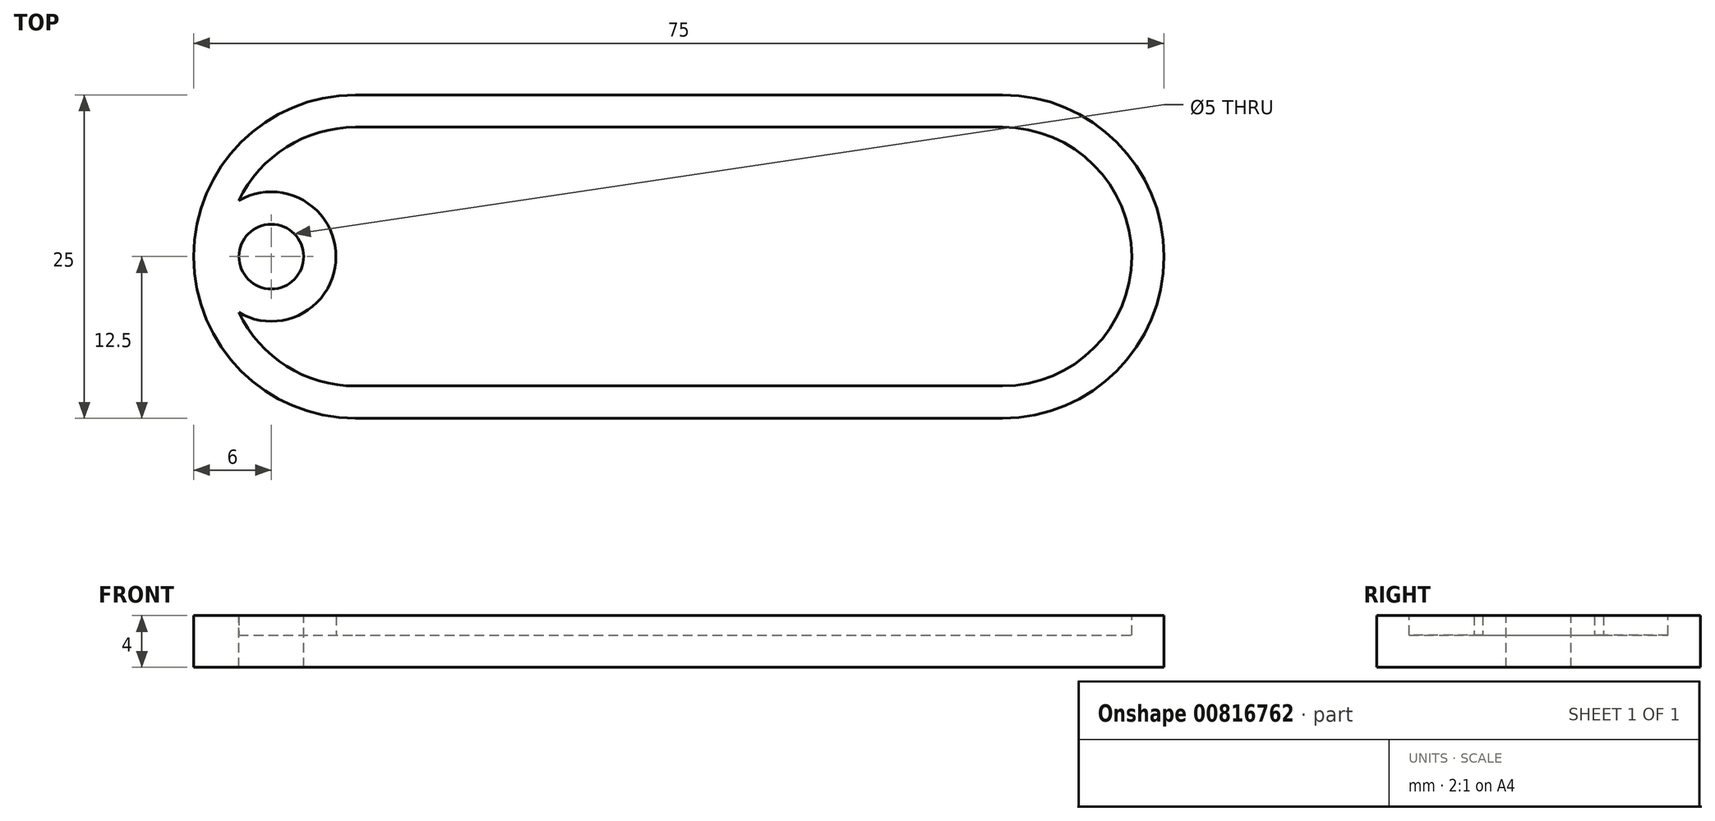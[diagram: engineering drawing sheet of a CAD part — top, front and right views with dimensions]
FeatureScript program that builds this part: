
annotation { "Feature Type Name" : "Feature", "Feature Type Description" : "" }
export const myFeature = defineFeature(function(context is Context, id is Id, definition is map)
    precondition{}
    {
        {
            var Q0;
            Q0=qCreatedBy(makeId("Top.planeOp"),FACE);
            var sketch = newSketch(context, id + "F0", { "sketchPlane" : qUnion([Q0])});
            skLineSegment(sketch, "E0.bottom", {"start": v(0, 0) * mm, "end": v(62.5, 0) * mm});
            skLineSegment(sketch, "E0.top", {"start": v(12.5, 25) * mm, "end": v(62.5, 25) * mm});
            skArc(sketch, "E1", {"start": v(12.5, 25) * mm, "mid": v(0, 12.5) * mm, "end": v(12.5, 0) * mm});
            skPoint(sketch, "E1.centerSnap0", {"position": v(0, 12.5) * mm});
            skArc(sketch, "E2", {"start": v(62.5, 0) * mm, "mid": v(75, 12.5) * mm, "end": v(62.5, 25) * mm});
            skPoint(sketch, "E2.centerSnap0", {"position": v(75, 12.5) * mm});
            skPoint(sketch, "E3.orphan", {"position": v(75, 0) * mm});
            skPoint(sketch, "E0.right.end.orphan", {"position": v(75, 25) * mm});
            skPoint(sketch, "E0.left.end.orphan", {"position": v(0, 25) * mm});
            skSolve(sketch);
        }
        {
            var Q0;
            Q0 = qSketchRegion(id + "F0", true);
            extrude(context, id + "F1", {"entities" : qUnion([Q0]), "depth" : 4 * mm, "offsetDistance" : 25 * mm});
        }
        {
            var Q0;
            Q0=makeQuery(id+"F1.opExtrude","CAP_FACE",FACE,{"disambiguationData":[OSD([sQuery(id+"F0.wireOp",EDGE,"E0.bottom"),sQuery(id+"F0.wireOp",EDGE,"E0.top"),sQuery(id+"F0.wireOp",EDGE,"E1"),sQuery(id+"F0.wireOp",EDGE,"E2")])],"isStart":false});
            var sketch = newSketch(context, id + "F2", { "sketchPlane" : qUnion([Q0])});
            skArc(sketch, "E4", {"start": v(12.5, 22.5) * mm, "mid": v(2.5, 12.5) * mm, "end": v(12.5, 2.5) * mm});
            skArc(sketch, "E5", {"start": v(62.5, 2.5) * mm, "mid": v(72.5, 12.5) * mm, "end": v(62.5, 22.5) * mm});
            skLineSegment(sketch, "E6", {"start": v(12.5, 22.5) * mm, "end": v(62.5, 22.5) * mm});
            skLineSegment(sketch, "E7", {"start": v(62.5, 2.5) * mm, "end": v(12.5, 2.5) * mm});
            skSolve(sketch);
        }
        {
            var Q0;
            Q0=makeQuery(id+"F2.imprint","IMPRINT",FACE,{"disambiguationData":[TD([[makeQuery(id+"F2.imprint","IMPRINT",EDGE,{"derivedFrom":sQuery(id+"F2.wireOp",EDGE,"E4")}),1.0]])]});
            extrude(context, id + "F3", {"entities" : qUnion([Q0]), "operationType" : NewBodyOperationType.REMOVE, "oppositeDirection" : true, "depth" : 1.5 * mm, "offsetDistance" : 25 * mm});
        }
        {
            var Q0;
            Q0=makeQuery(id+"F3.boolean.opBoolean","COPY",FACE,{"derivedFrom":makeQuery(id+"F3.opExtrude","CAP_FACE",FACE,{"disambiguationData":[OSD([sQuery(id+"F2.wireOp",EDGE,"E4"),sQuery(id+"F2.wireOp",EDGE,"E5"),sQuery(id+"F2.wireOp",EDGE,"E6"),sQuery(id+"F2.wireOp",EDGE,"E7")])],"isStart":false})});
            var sketch = newSketch(context, id + "F4", { "sketchPlane" : qUnion([Q0])});
            skCircle(sketch, "E8", {"center": v(6, 12.5) * mm, "radius": 5 * mm});
            skPoint(sketch, "E8.centerSnap0", {"position": v(2.5, 12.5) * mm});
            skSolve(sketch);
        }
        {
            var Q0;
            {var subQ0=sQuery(id+"F4.wireOp",EDGE,"E8");var subQ1=makeQuery(id+"F3.boolean.opBoolean","COPY",EDGE,{"derivedFrom":makeQuery(id+"F3.opExtrude","CAP_EDGE",EDGE,{"disambiguationData":[OSD([sQuery(id+"F2.wireOp",EDGE,"E4")])],"isStart":false})});var subQ2=makeQuery(id+"F4.imprint","INTERSECT",VERTEX,{"disambiguationData":[OD(0.0)],"derivedFrom":[subQ1,subQ0]});Q0=makeQuery(id+"F4.imprint","IMPRINT",FACE,{"disambiguationData":[TD([[makeQuery(id+"F4.imprint","IMPRINT",EDGE,{"disambiguationData":[TD([[subQ2,-1.0]])],"derivedFrom":subQ0}),1.0]])]});}
            extrude(context, id + "F5", {"entities" : qUnion([Q0]), "operationType" : NewBodyOperationType.ADD, "depth" : 1.5 * mm, "offsetDistance" : 25 * mm});
        }
        {
            var Q0;
            {var subQ0=sQuery(id+"F4.wireOp",EDGE,"E8");var subQ1=makeQuery(id+"F3.boolean.opBoolean","COPY",EDGE,{"derivedFrom":makeQuery(id+"F3.opExtrude","CAP_EDGE",EDGE,{"disambiguationData":[OSD([sQuery(id+"F2.wireOp",EDGE,"E4")])],"isStart":false})});var subQ2=makeQuery(id+"F4.imprint","INTERSECT",VERTEX,{"disambiguationData":[OD(0.0)],"derivedFrom":[subQ1,subQ0]});Q0=makeQuery(id+"F4.imprint","IMPRINT",FACE,{"disambiguationData":[TD([[makeQuery(id+"F4.imprint","IMPRINT",EDGE,{"disambiguationData":[TD([[subQ2,1.0]])],"derivedFrom":subQ0}),1.0]])]});}
            extrude(context, id + "F6", {"entities" : qUnion([Q0]), "operationType" : NewBodyOperationType.ADD, "depth" : 1.5 * mm, "offsetDistance" : 25 * mm});
        }
        {
            var Q0;
            Q0=makeQuery(id+"F6.boolean.opBoolean","MERGE",FACE,{"derivedFrom":[makeQuery(id+"F1.opExtrude","CAP_FACE",FACE,{"disambiguationData":[OSD([sQuery(id+"F0.wireOp",EDGE,"E0.bottom"),sQuery(id+"F0.wireOp",EDGE,"E0.top"),sQuery(id+"F0.wireOp",EDGE,"E1"),sQuery(id+"F0.wireOp",EDGE,"E2")])],"isStart":false}),makeQuery(id+"F6.opExtrude","CAP_FACE",FACE,{"disambiguationData":[OSD([sQuery(id+"F2.wireOp",EDGE,"E4"),sQuery(id+"F4.wireOp",EDGE,"E8")])],"isStart":false})]});
            var sketch = newSketch(context, id + "F7", { "sketchPlane" : qUnion([Q0])});
            skCircle(sketch, "E9", {"center": v(6, 12.5) * mm, "radius": 2.5 * mm});
            skSolve(sketch);
        }
        {
            var Q0;
            Q0=makeQuery(id+"F7.imprint","IMPRINT",FACE,{"disambiguationData":[TD([[makeQuery(id+"F7.imprint","IMPRINT",EDGE,{"derivedFrom":sQuery(id+"F7.wireOp",EDGE,"E9")}),1.0]])]});
            extrude(context, id + "F8", {"entities" : qUnion([Q0]), "operationType" : NewBodyOperationType.REMOVE, "oppositeDirection" : true, "depth" : 25 * mm, "offsetDistance" : 25 * mm});
        }
    });
